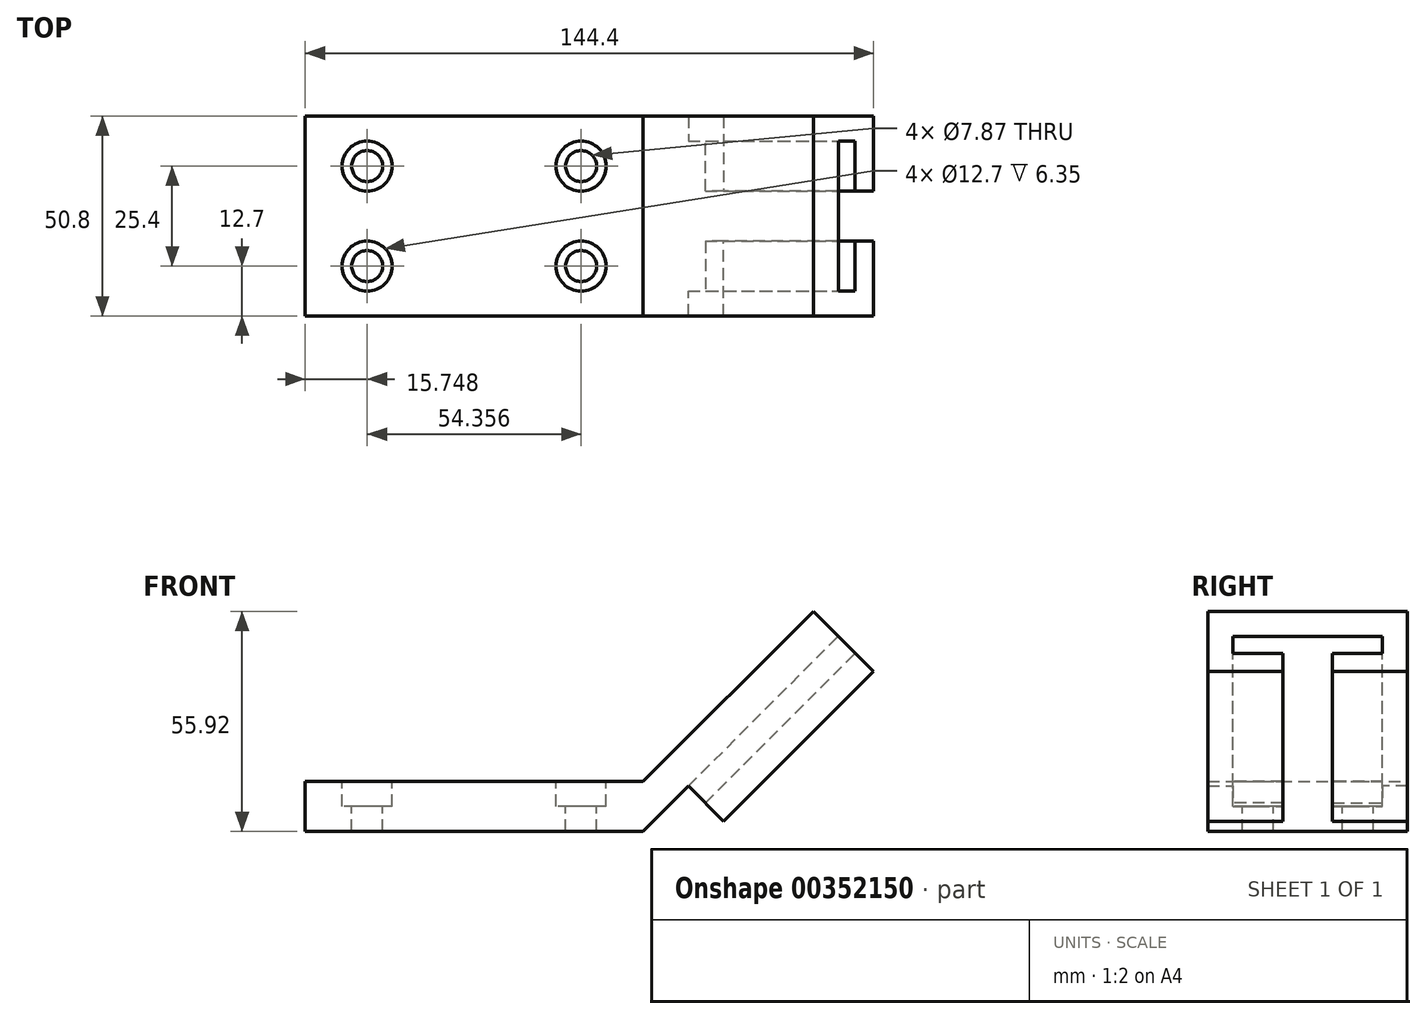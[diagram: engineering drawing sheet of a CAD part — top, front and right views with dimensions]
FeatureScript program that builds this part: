
annotation { "Feature Type Name" : "Feature", "Feature Type Description" : "" }
export const myFeature = defineFeature(function(context is Context, id is Id, definition is map)
    precondition{}
    {
        {
            var Q0;
            Q0=qCreatedBy(makeId("Front.planeOp"),FACE);
            var sketch = newSketch(context, id + "F0", { "sketchPlane" : qUnion([Q0])});
            skLineSegment(sketch, "E0.bottom", {"start": v(0, 0) * mm, "end": v(85.85, 0) * mm});
            skLineSegment(sketch, "E0.top", {"start": v(0, 12.7) * mm, "end": v(85.85, 12.7) * mm});
            skLineSegment(sketch, "E0.left", {"start": v(0, 0) * mm, "end": v(0, 12.7) * mm});
            skLineSegment(sketch, "E0.right", {"start": v(85.85, 0) * mm, "end": v(85.85, 12.7) * mm});
            skLineSegment(sketch, "E1", {"start": v(85.85, 12.7) * mm, "end": v(129.07, 55.92) * mm});
            skLineSegment(sketch, "E2", {"start": v(85.85, 0) * mm, "end": v(135.42, 49.57) * mm});
            skLineSegment(sketch, "E3", {"start": v(135.42, 49.57) * mm, "end": v(129.07, 55.92) * mm});
            skSolve(sketch);
        }
        {
            var Q0;
            Q0 = qSketchRegion(id + "F0", true);
            extrude(context, id + "F1", {"entities" : qUnion([Q0]), "depth" : 50.8 * mm});
        }
        {
            var Q0;
            Q0=makeQuery(id+"F1.opExtrude","SWEPT_FACE",FACE,{"disambiguationData":[OSD([sQuery(id+"F0.wireOp",EDGE,"E0.top")])]});
            var sketch = newSketch(context, id + "F2", { "sketchPlane" : qUnion([Q0])});
            skPoint(sketch, "E4", {"position": v(15.75, -12.7) * mm});
            skPoint(sketch, "E5", {"position": v(70.1, -12.7) * mm});
            skPoint(sketch, "E6", {"position": v(15.75, -38.1) * mm});
            skPoint(sketch, "E7", {"position": v(70.1, -38.1) * mm});
            skSolve(sketch);
        }
        {
            var Q0;
            Q0=sQuery(id+"F2.wireOp",VERTEX,"E4");
            var Q1;
            Q1=sQuery(id+"F2.wireOp",VERTEX,"E6");
            var Q2;
            Q2=sQuery(id+"F2.wireOp",VERTEX,"E7");
            var Q3;
            Q3=sQuery(id+"F2.wireOp",VERTEX,"E5");
            var Q4;
            Q4=makeQuery(id+"F1.opExtrude","SWEPT_BODY",BODY,{"disambiguationData":[OSD([sQuery(id+"F0.wireOp",EDGE,"E0.bottom"),sQuery(id+"F0.wireOp",EDGE,"E0.top"),sQuery(id+"F0.wireOp",EDGE,"E0.left"),sQuery(id+"F0.wireOp",EDGE,"E0.right")])]});
            hole(context, id + "F3", {"style" : HoleStyle.C_BORE, "endStyle" : HoleEndStyle.THROUGH, "holeDiameter" : 7.87 * mm, "cBoreDiameter" : 12.7 * mm, "cBoreDepth" : 6.35 * mm, "isTappedThrough" : true, "tappedDepth" : 12.7 * mm, "tapClearance" : 3, "locations" : qUnion([Q0, Q1, Q2, Q3]), "scope" : qUnion([Q4])});
        }
        {
            var Q0;
            Q0=makeQuery(id+"F0.imprint","IMPRINT",FACE,{"disambiguationData":[TD([[makeQuery(id+"F0.imprint","IMPRINT",EDGE,{"derivedFrom":sQuery(id+"F0.wireOp",EDGE,"E0.right")}),-1.0]])]});
            extrude(context, id + "F4", {"entities" : qUnion([Q0]), "operationType" : NewBodyOperationType.ADD, "depth" : 25.4 * mm});
        }
        {
            var Q0;
            Q0=makeQuery(id+"F1.opExtrude","SWEPT_FACE",FACE,{"disambiguationData":[OSD([sQuery(id+"F0.wireOp",EDGE,"E2")])]});
            var sketch = newSketch(context, id + "F5", { "sketchPlane" : qUnion([Q0])});
            skLineSegment(sketch, "E8.bottom", {"start": v(0, 130.81) * mm, "end": v(-19.05, 130.81) * mm});
            skLineSegment(sketch, "E8.top", {"start": v(0, 76.96) * mm, "end": v(-19.05, 76.96) * mm});
            skLineSegment(sketch, "E8.left", {"start": v(0, 130.81) * mm, "end": v(0, 76.96) * mm});
            skLineSegment(sketch, "E8.right", {"start": v(-19.05, 130.81) * mm, "end": v(-19.05, 76.96) * mm});
            skLineSegment(sketch, "E9.bottom", {"start": v(-50.8, 130.81) * mm, "end": v(-31.75, 130.81) * mm});
            skLineSegment(sketch, "E9.top", {"start": v(-50.8, 76.96) * mm, "end": v(-31.75, 76.96) * mm});
            skLineSegment(sketch, "E9.left", {"start": v(-50.8, 130.81) * mm, "end": v(-50.8, 76.96) * mm});
            skLineSegment(sketch, "E9.right", {"start": v(-31.75, 130.81) * mm, "end": v(-31.75, 76.96) * mm});
            skSolve(sketch);
        }
        {
            var Q0;
            Q0=makeQuery(id+"F5.imprint","IMPRINT",FACE,{"disambiguationData":[TD([[makeQuery(id+"F5.imprint","IMPRINT",EDGE,{"derivedFrom":sQuery(id+"F5.wireOp",EDGE,"E8.bottom")}),-1.0]])]});
            var Q1;
            Q1=makeQuery(id+"F5.imprint","IMPRINT",FACE,{"disambiguationData":[TD([[makeQuery(id+"F5.imprint","IMPRINT",EDGE,{"derivedFrom":sQuery(id+"F5.wireOp",EDGE,"E9.bottom")}),-1.0]])]});
            extrude(context, id + "F6", {"entities" : qUnion([Q0, Q1]), "operationType" : NewBodyOperationType.ADD, "depth" : 12.7 * mm});
        }
        {
            var Q0;
            Q0=makeQuery(id+"F6.boolean.opBoolean","MERGE",FACE,{"derivedFrom":[makeQuery(id+"F1.opExtrude","SWEPT_FACE",FACE,{"disambiguationData":[OSD([sQuery(id+"F0.wireOp",EDGE,"E3")])]}),makeQuery(id+"F6.opExtrude","SWEPT_FACE",FACE,{"disambiguationData":[OSD([sQuery(id+"F5.wireOp",EDGE,"E8.bottom")])]}),makeQuery(id+"F6.opExtrude","SWEPT_FACE",FACE,{"disambiguationData":[OSD([sQuery(id+"F5.wireOp",EDGE,"E9.bottom")])]})]});
            var sketch = newSketch(context, id + "F7", { "sketchPlane" : qUnion([Q0])});
            skLineSegment(sketch, "E10.bottom", {"start": v(-19.05, -60.7) * mm, "end": v(-6.35, -60.7) * mm});
            skLineSegment(sketch, "E10.top", {"start": v(-19.05, -66.8) * mm, "end": v(-6.35, -66.8) * mm});
            skLineSegment(sketch, "E10.left", {"start": v(-19.05, -60.7) * mm, "end": v(-19.05, -66.8) * mm});
            skLineSegment(sketch, "E10.right", {"start": v(-6.35, -60.7) * mm, "end": v(-6.35, -66.8) * mm});
            skLineSegment(sketch, "E11.bottom", {"start": v(-31.75, -60.7) * mm, "end": v(-44.45, -60.7) * mm});
            skLineSegment(sketch, "E11.top", {"start": v(-31.75, -66.8) * mm, "end": v(-44.45, -66.8) * mm});
            skLineSegment(sketch, "E11.left", {"start": v(-31.75, -60.7) * mm, "end": v(-31.75, -66.8) * mm});
            skLineSegment(sketch, "E11.right", {"start": v(-44.45, -60.7) * mm, "end": v(-44.45, -66.8) * mm});
            skSolve(sketch);
        }
        {
            var Q0;
            Q0 = qSketchRegion(id + "F7", true);
            extrude(context, id + "F8", {"entities" : qUnion([Q0]), "operationType" : NewBodyOperationType.REMOVE, "oppositeDirection" : true, "depth" : 53.85 * mm});
        }
    });
